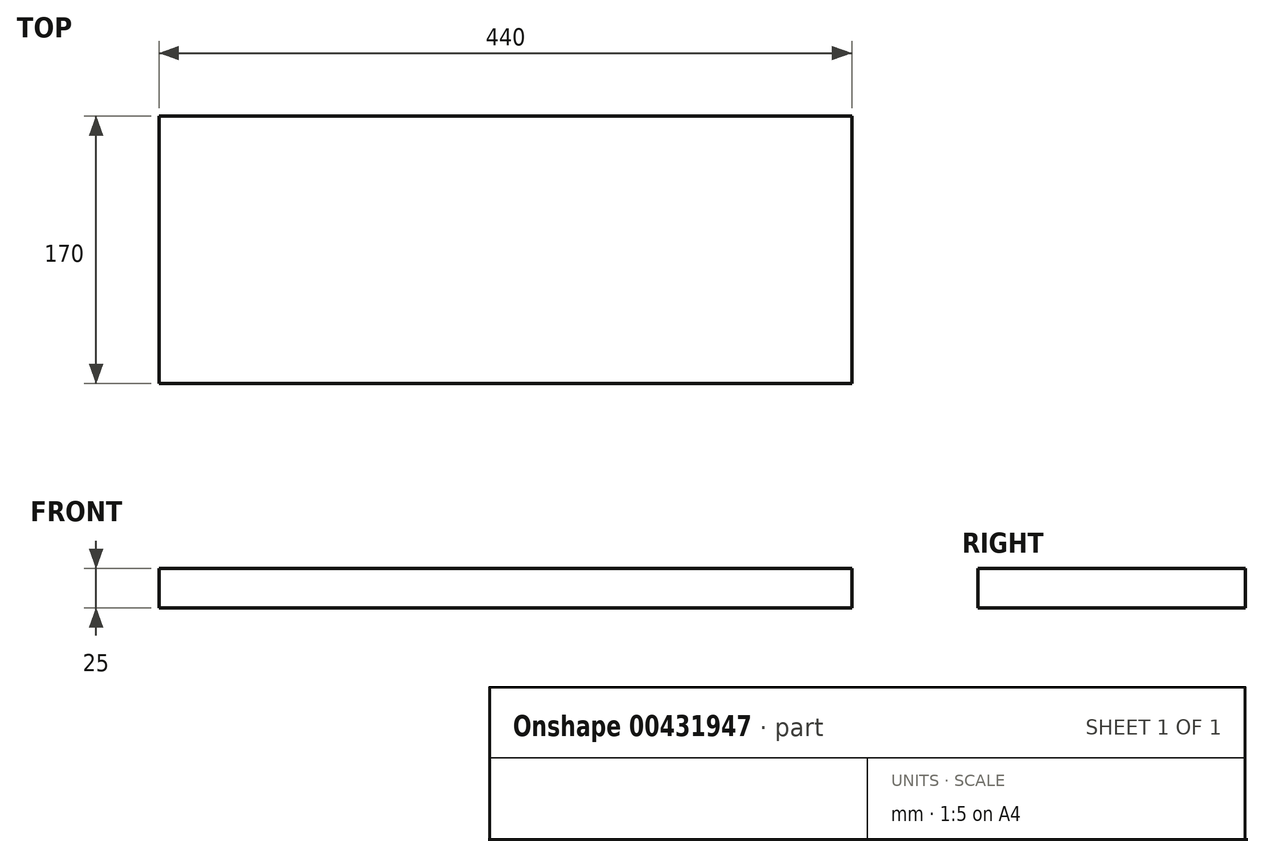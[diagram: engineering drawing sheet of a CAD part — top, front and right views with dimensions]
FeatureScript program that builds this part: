
annotation { "Feature Type Name" : "Feature", "Feature Type Description" : "" }
export const myFeature = defineFeature(function(context is Context, id is Id, definition is map)
    precondition{}
    {
        {
            var Q0;
            Q0=qCreatedBy(makeId("Top.planeOp"),FACE);
            var sketch = newSketch(context, id + "F0", { "sketchPlane" : qUnion([Q0])});
            skLineSegment(sketch, "E0.bottom", {"start": v(-220, 85) * mm, "end": v(220, 85) * mm});
            skLineSegment(sketch, "E0.top", {"start": v(-220, -85) * mm, "end": v(220, -85) * mm});
            skLineSegment(sketch, "E0.left", {"start": v(-220, 85) * mm, "end": v(-220, -85) * mm});
            skLineSegment(sketch, "E0.right", {"start": v(220, 85) * mm, "end": v(220, -85) * mm});
            skPoint(sketch, "E0.middle", {"position": v(0, 0) * mm});
            skSolve(sketch);
        }
        {
            var Q0;
            Q0 = qSketchRegion(id + "F0", true);
            extrude(context, id + "F1", {"entities" : qUnion([Q0]), "depth" : 25 * mm, "offsetDistance" : 25 * mm});
        }
    });
